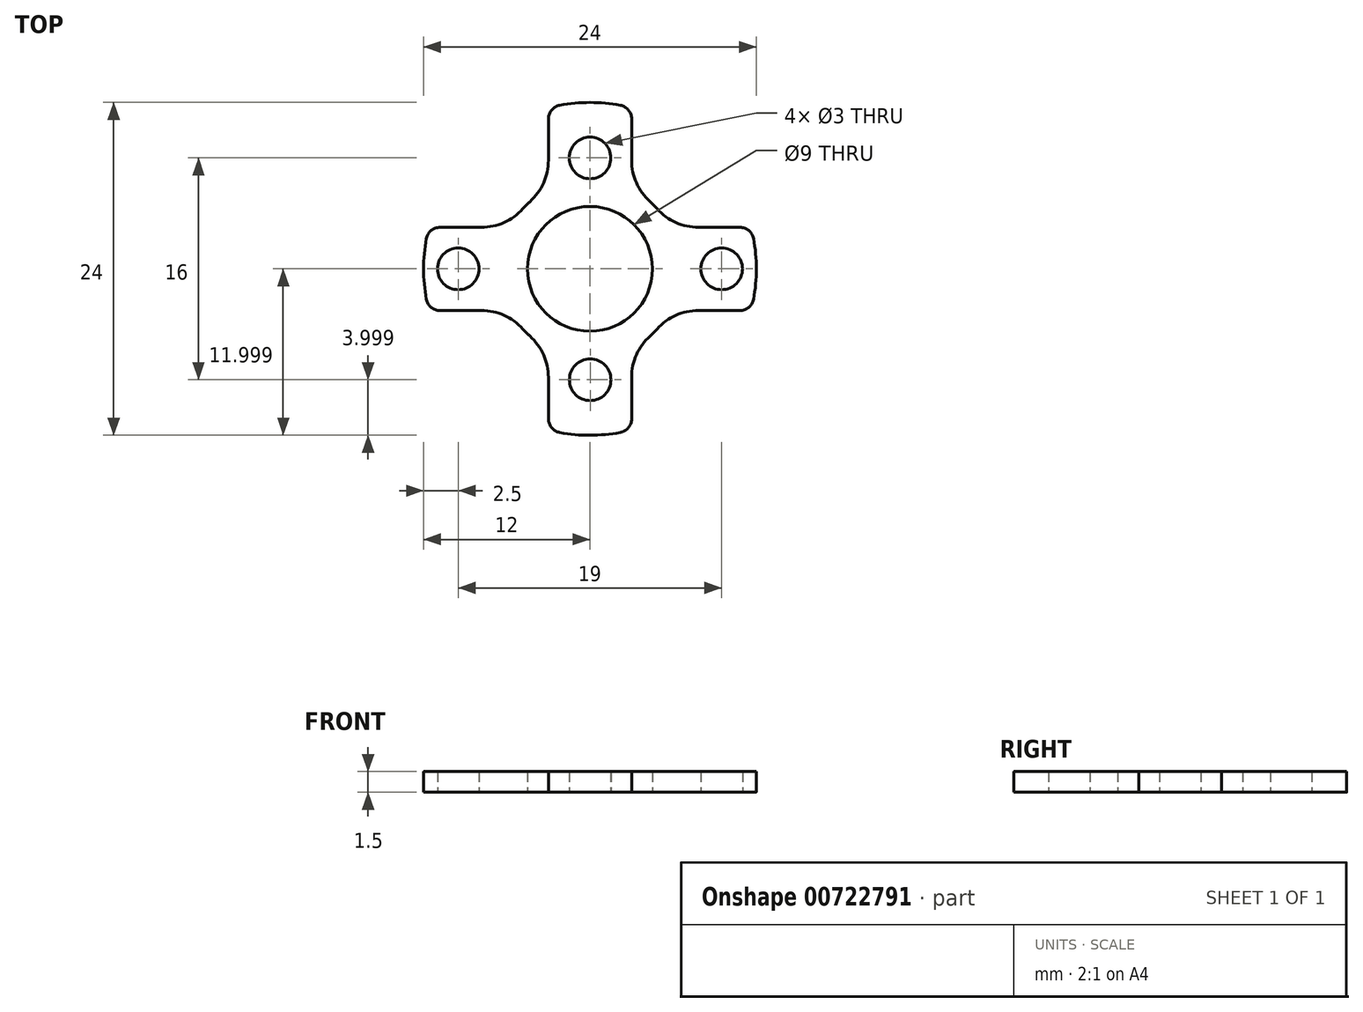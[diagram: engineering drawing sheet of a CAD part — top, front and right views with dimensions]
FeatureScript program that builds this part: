
annotation { "Feature Type Name" : "Feature", "Feature Type Description" : "" }
export const myFeature = defineFeature(function(context is Context, id is Id, definition is map)
    precondition{}
    {
        {
            var Q0;
            Q0=qCreatedBy(makeId("Top.planeOp"),FACE);
            var sketch = newSketch(context, id + "F0", { "sketchPlane" : qUnion([Q0])});
            skCircle(sketch, "E0.MirrorC", {"center": v(0.01, -8.03) * mm, "radius": 1.5 * mm});
            skCircle(sketch, "E1.MirrorC", {"center": v(-9.5, -0.03) * mm, "radius": 1.5 * mm});
            skCircle(sketch, "E2.MirrorC", {"center": v(0, 7.97) * mm, "radius": 1.5 * mm});
            skCircle(sketch, "E3.MirrorC", {"center": v(9.5, -0.03) * mm, "radius": 1.5 * mm});
            skCircle(sketch, "E4.MirrorC", {"center": v(0, -0.03) * mm, "radius": 9.5 * mm, "construction": true});
            skLineSegment(sketch, "E5.MirrorCS", {"start": v(24.06, -0.03) * mm, "end": v(-12.27, -0.03) * mm, "construction": true});
            skLineSegment(sketch, "E6.MirrorCS", {"start": v(-8.84, 8.8) * mm, "end": v(8.84, -8.87) * mm, "construction": true});
            skCircle(sketch, "E7.MirrorC", {"center": v(0, -0.03) * mm, "radius": 8 * mm, "construction": true});
            skCircle(sketch, "E8", {"center": v(0, -0.03) * mm, "radius": 4.5 * mm});
            skLineSegment(sketch, "E9", {"start": v(-3, 10.79) * mm, "end": v(-3, 5.74) * mm});
            skLineSegment(sketch, "E10", {"start": v(3, 10.78) * mm, "end": v(3, 5.73) * mm});
            skArc(sketch, "E11", {"start": v(-11.8, 2.15) * mm, "mid": v(-12, -0.04) * mm, "end": v(-11.8, -2.22) * mm});
            skPoint(sketch, "E12.orphan", {"position": v(-3, 7.97) * mm});
            skPoint(sketch, "E13.orphan", {"position": v(3, 7.97) * mm});
            skPoint(sketch, "E14.orphan", {"position": v(3, -11.22) * mm});
            skPoint(sketch, "E15.orphan", {"position": v(-3, -11.22) * mm});
            skLineSegment(sketch, "E16.MirrorCS", {"start": v(-10.82, 2.96) * mm, "end": v(-5.77, 2.96) * mm});
            skLineSegment(sketch, "E17.MirrorCS", {"start": v(-10.82, -3.04) * mm, "end": v(-5.76, -3.04) * mm});
            skArc(sketch, "E18.trimOffspring", {"start": v(2.19, 11.77) * mm, "mid": v(0, 11.97) * mm, "end": v(-2.18, 11.77) * mm});
            skArc(sketch, "E19.trimOffspring", {"start": v(11.8, -2.22) * mm, "mid": v(12, -0.04) * mm, "end": v(11.8, 2.15) * mm});
            skArc(sketch, "E20.trimOffspring", {"start": v(-2.18, -11.83) * mm, "mid": v(0, -12.03) * mm, "end": v(2.19, -11.83) * mm});
            skPoint(sketch, "E21.visualSharp", {"position": v(-3, 11.59) * mm});
            skArc(sketch, "E21.filletArc", {"start": v(-2.18, 11.77) * mm, "mid": v(-2.76, 11.43) * mm, "end": v(-3, 10.79) * mm});
            skPoint(sketch, "E22.visualSharp", {"position": v(3, 11.59) * mm});
            skArc(sketch, "E22.filletArc", {"start": v(3, 10.78) * mm, "mid": v(2.77, 11.42) * mm, "end": v(2.19, 11.77) * mm});
            skPoint(sketch, "E23.visualSharp", {"position": v(3, -11.65) * mm});
            skArc(sketch, "E23.filletArc", {"start": v(2.19, -11.83) * mm, "mid": v(2.77, -11.49) * mm, "end": v(3, -10.85) * mm});
            skPoint(sketch, "E24.visualSharp", {"position": v(-3, -11.65) * mm});
            skArc(sketch, "E24.filletArc", {"start": v(-3, -10.85) * mm, "mid": v(-2.76, -11.49) * mm, "end": v(-2.18, -11.83) * mm});
            skPoint(sketch, "E25.visualSharp", {"position": v(11.62, -3.04) * mm});
            skArc(sketch, "E25.filletArc", {"start": v(10.82, -3.04) * mm, "mid": v(11.46, -2.8) * mm, "end": v(11.8, -2.22) * mm});
            skPoint(sketch, "E26.visualSharp", {"position": v(11.62, 2.96) * mm});
            skArc(sketch, "E26.filletArc", {"start": v(11.8, 2.15) * mm, "mid": v(11.46, 2.73) * mm, "end": v(10.82, 2.96) * mm});
            skPoint(sketch, "E27.visualSharp", {"position": v(-11.62, 2.96) * mm});
            skArc(sketch, "E27.filletArc", {"start": v(-10.82, 2.96) * mm, "mid": v(-11.46, 2.73) * mm, "end": v(-11.8, 2.15) * mm});
            skPoint(sketch, "E28.visualSharp", {"position": v(-11.62, -3.04) * mm});
            skArc(sketch, "E28.filletArc", {"start": v(-11.8, -2.22) * mm, "mid": v(-11.46, -2.8) * mm, "end": v(-10.82, -3.04) * mm});
            skCircle(sketch, "E29", {"center": v(0, -0.03) * mm, "radius": 6.5 * mm});
            skLineSegment(sketch, "E30.trimOffspring", {"start": v(-3, -5.8) * mm, "end": v(-3, -10.85) * mm});
            skLineSegment(sketch, "E31.trimOffspring", {"start": v(3, -5.8) * mm, "end": v(3, -10.85) * mm});
            skLineSegment(sketch, "E32.trimOffspring", {"start": v(5.76, -3.04) * mm, "end": v(10.82, -3.04) * mm});
            skLineSegment(sketch, "E33.trimOffspring", {"start": v(5.77, 2.96) * mm, "end": v(10.82, 2.96) * mm});
            skSolve(sketch);
        }
        {
            var Q0;
            Q0 = qSketchRegion(id + "F0", true);
            extrude(context, id + "F1", {"entities" : qUnion([Q0]), "depth" : 1.5 * mm, "offsetDistance" : 25 * mm});
        }
        {
            var Q0;
            Q0=makeQuery(id+"F1.opExtrude","SWEPT_EDGE",EDGE,{"disambiguationData":[OSD([sQuery(id+"F0.wireOp",EDGE,"E17.MirrorCS"),sQuery(id+"F0.wireOp",EDGE,"E29")])]});
            var Q1;
            Q1=makeQuery(id+"F1.opExtrude","SWEPT_EDGE",EDGE,{"disambiguationData":[OSD([sQuery(id+"F0.wireOp",EDGE,"E29"),sQuery(id+"F0.wireOp",EDGE,"E30.trimOffspring")])]});
            var Q2;
            Q2=makeQuery(id+"F1.opExtrude","SWEPT_EDGE",EDGE,{"disambiguationData":[OSD([sQuery(id+"F0.wireOp",EDGE,"E10"),sQuery(id+"F0.wireOp",EDGE,"E29")])]});
            var Q3;
            Q3=makeQuery(id+"F1.opExtrude","SWEPT_EDGE",EDGE,{"disambiguationData":[OSD([sQuery(id+"F0.wireOp",EDGE,"E29"),sQuery(id+"F0.wireOp",EDGE,"E33.trimOffspring")])]});
            var Q4;
            Q4=makeQuery(id+"F1.opExtrude","SWEPT_EDGE",EDGE,{"disambiguationData":[OSD([sQuery(id+"F0.wireOp",EDGE,"E29"),sQuery(id+"F0.wireOp",EDGE,"E32.trimOffspring")])]});
            var Q5;
            Q5=makeQuery(id+"F1.opExtrude","SWEPT_EDGE",EDGE,{"disambiguationData":[OSD([sQuery(id+"F0.wireOp",EDGE,"E29"),sQuery(id+"F0.wireOp",EDGE,"E31.trimOffspring")])]});
            var Q6;
            Q6=makeQuery(id+"F1.opExtrude","SWEPT_EDGE",EDGE,{"disambiguationData":[OSD([sQuery(id+"F0.wireOp",EDGE,"E9"),sQuery(id+"F0.wireOp",EDGE,"E29")])]});
            var Q7;
            Q7=makeQuery(id+"F1.opExtrude","SWEPT_EDGE",EDGE,{"disambiguationData":[OSD([sQuery(id+"F0.wireOp",EDGE,"E16.MirrorCS"),sQuery(id+"F0.wireOp",EDGE,"E29")])]});
            fillet(context, id + "F2", {"entities" : qUnion([Q0, Q1, Q2, Q3, Q4, Q5, Q6, Q7]), "radius" : 4 * mm, "tangentPropagation" : true, "allowEdgeOverflow" : false});
        }
    });
